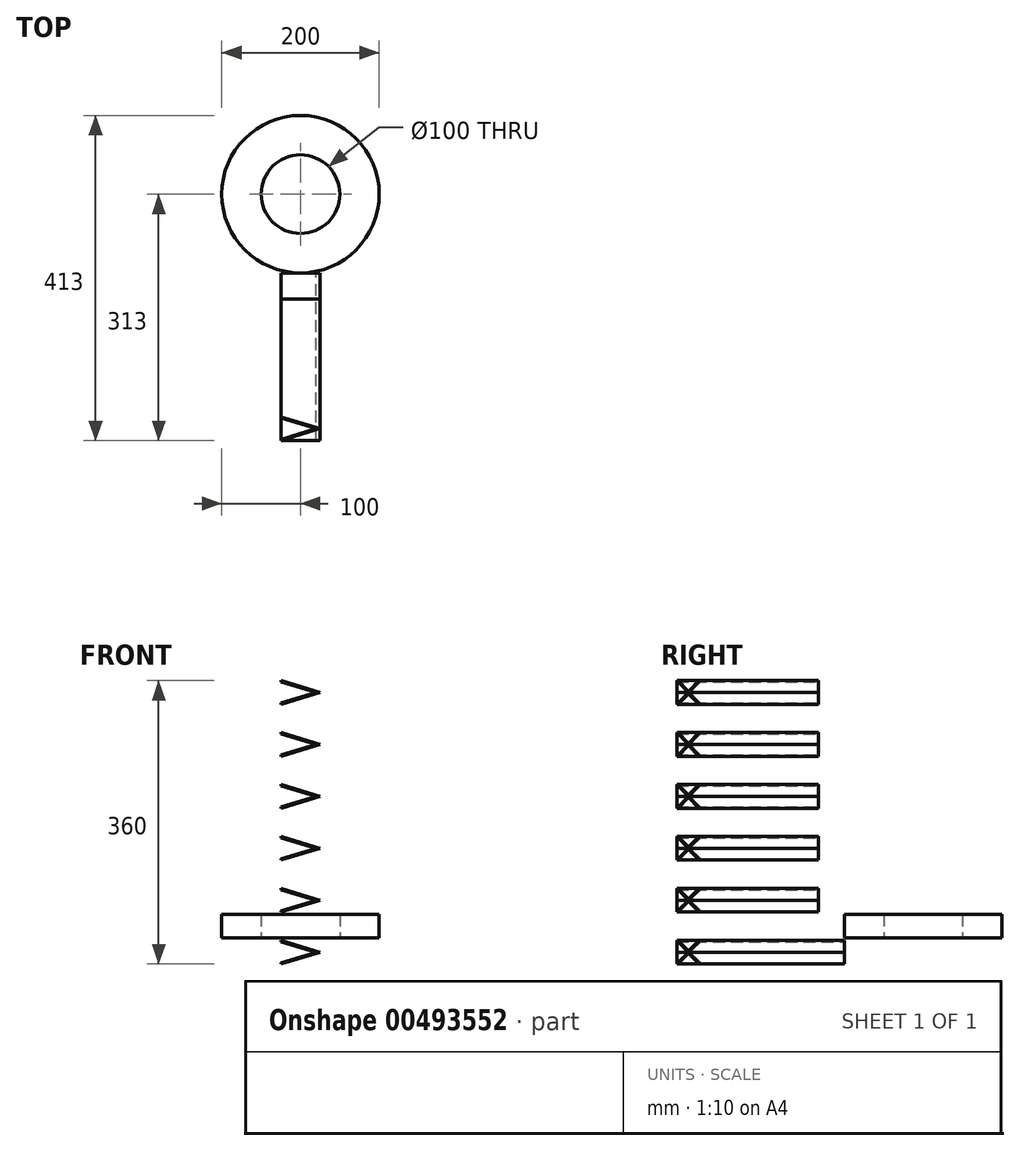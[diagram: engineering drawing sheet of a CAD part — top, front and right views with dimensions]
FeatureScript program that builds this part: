
annotation { "Feature Type Name" : "Feature", "Feature Type Description" : "" }
export const myFeature = defineFeature(function(context is Context, id is Id, definition is map)
    precondition{}
    {
        {
            var Q0;
            Q0=qCreatedBy(makeId("Right.planeOp"),FACE);
            var sketch = newSketch(context, id + "F0", { "sketchPlane" : qUnion([Q0])});
            skLineSegment(sketch, "E0", {"start": v(0, 0) * mm, "end": v(0, 400) * mm});
            skLineSegment(sketch, "E1", {"start": v(0, 0) * mm, "end": v(100, 0) * mm});
            skLineSegment(sketch, "E2", {"start": v(100, 0) * mm, "end": v(100, 360) * mm});
            skLineSegment(sketch, "E3.bottom", {"start": v(100, 360) * mm, "end": v(130, 360) * mm});
            skLineSegment(sketch, "E3.top", {"start": v(100, 0) * mm, "end": v(130, 0) * mm});
            skLineSegment(sketch, "E3.left", {"start": v(100, 360) * mm, "end": v(100, 0) * mm});
            skLineSegment(sketch, "E3.right", {"start": v(130, 360) * mm, "end": v(130, 0) * mm});
            skLineSegment(sketch, "E4.bottom", {"start": v(130, 0) * mm, "end": v(280, 0) * mm});
            skLineSegment(sketch, "E4.top", {"start": v(100, 30) * mm, "end": v(280, 30) * mm});
            skLineSegment(sketch, "E4.left", {"start": v(130, 0) * mm, "end": v(130, 30) * mm});
            skLineSegment(sketch, "E4.right", {"start": v(280, 0) * mm, "end": v(280, 30) * mm});
            skLineSegment(sketch, "E5", {"start": v(280, 66) * mm, "end": v(130, 66) * mm});
            skLineSegment(sketch, "E6", {"start": v(280, 66) * mm, "end": v(280, 96) * mm});
            skLineSegment(sketch, "E7.bottom", {"start": v(280, 96) * mm, "end": v(130, 96) * mm});
            skLineSegment(sketch, "E7.left", {"start": v(280, 96) * mm, "end": v(280, 66) * mm});
            skLineSegment(sketch, "E7.right", {"start": v(130, 96) * mm, "end": v(130, 66) * mm});
            skLineSegment(sketch, "E8.0.1.0", {"start": v(280, 132) * mm, "end": v(130, 132) * mm});
            skLineSegment(sketch, "E8.0.1.1", {"start": v(280, 132) * mm, "end": v(280, 162) * mm});
            skLineSegment(sketch, "E8.0.1.2", {"start": v(130, 162) * mm, "end": v(130, 132) * mm});
            skLineSegment(sketch, "E8.0.1.3", {"start": v(280, 162) * mm, "end": v(130, 162) * mm});
            skLineSegment(sketch, "E8.0.1.4", {"start": v(280, 162) * mm, "end": v(280, 132) * mm});
            skLineSegment(sketch, "E8.0.1.5", {"start": v(280, 132) * mm, "end": v(130, 132) * mm});
            skLineSegment(sketch, "E8.0.2.0", {"start": v(280, 198) * mm, "end": v(130, 198) * mm});
            skLineSegment(sketch, "E8.0.2.1", {"start": v(280, 198) * mm, "end": v(280, 228) * mm});
            skLineSegment(sketch, "E8.0.2.2", {"start": v(130, 228) * mm, "end": v(130, 198) * mm});
            skLineSegment(sketch, "E8.0.2.3", {"start": v(280, 228) * mm, "end": v(130, 228) * mm});
            skLineSegment(sketch, "E8.0.2.4", {"start": v(280, 228) * mm, "end": v(280, 198) * mm});
            skLineSegment(sketch, "E8.0.2.5", {"start": v(280, 198) * mm, "end": v(130, 198) * mm});
            skLineSegment(sketch, "E8.0.3.0", {"start": v(280, 264) * mm, "end": v(130, 264) * mm});
            skLineSegment(sketch, "E8.0.3.1", {"start": v(280, 264) * mm, "end": v(280, 294) * mm});
            skLineSegment(sketch, "E8.0.3.2", {"start": v(130, 294) * mm, "end": v(130, 264) * mm});
            skLineSegment(sketch, "E8.0.3.3", {"start": v(280, 294) * mm, "end": v(130, 294) * mm});
            skLineSegment(sketch, "E8.0.3.4", {"start": v(280, 294) * mm, "end": v(280, 264) * mm});
            skLineSegment(sketch, "E8.0.3.5", {"start": v(280, 264) * mm, "end": v(130, 264) * mm});
            skLineSegment(sketch, "E8.0.4.0", {"start": v(280, 330) * mm, "end": v(100, 330) * mm});
            skLineSegment(sketch, "E8.0.4.1", {"start": v(280, 330) * mm, "end": v(280, 360) * mm});
            skLineSegment(sketch, "E8.0.4.2", {"start": v(130, 360) * mm, "end": v(130, 330) * mm});
            skLineSegment(sketch, "E8.0.4.3", {"start": v(280, 360) * mm, "end": v(130, 360) * mm});
            skLineSegment(sketch, "E8.0.4.4", {"start": v(280, 360) * mm, "end": v(280, 330) * mm});
            skLineSegment(sketch, "E8.0.4.5", {"start": v(280, 330) * mm, "end": v(130, 330) * mm});
            skLineSegment(sketch, "E8.direction1", {"start": v(130, 66) * mm, "end": v(205, 66) * mm, "construction": true});
            skLineSegment(sketch, "E8.direction2", {"start": v(130, 66) * mm, "end": v(130, 132) * mm, "construction": true});
            skLineSegment(sketch, "E9", {"start": v(-100, 363) * mm, "end": v(-283, 363) * mm});
            skLineSegment(sketch, "E10", {"start": v(-100, 363) * mm, "end": v(-100, 393) * mm});
            skLineSegment(sketch, "E11.bottom", {"start": v(-283, 363) * mm, "end": v(-100, 363) * mm});
            skLineSegment(sketch, "E11.top", {"start": v(-313, 393) * mm, "end": v(-100, 393) * mm});
            skLineSegment(sketch, "E12.MirrorCS", {"start": v(-100, -3) * mm, "end": v(-100, -33) * mm});
            skLineSegment(sketch, "E13.MirrorCS", {"start": v(-283, -3) * mm, "end": v(-100, -3) * mm});
            skLineSegment(sketch, "E14.MirrorCS", {"start": v(-100, -3) * mm, "end": v(-283, -3) * mm});
            skLineSegment(sketch, "E15.MirrorCS", {"start": v(-313, -33) * mm, "end": v(-100, -33) * mm});
            skLineSegment(sketch, "E16", {"start": v(-283, 363) * mm, "end": v(-283, 327) * mm});
            skLineSegment(sketch, "E17.0", {"start": v(-133, 297) * mm, "end": v(-283, 297) * mm});
            skLineSegment(sketch, "E18.0", {"start": v(-133, 327) * mm, "end": v(-283, 327) * mm});
            skLineSegment(sketch, "E19.0", {"start": v(-313, 393) * mm, "end": v(-313, -33) * mm});
            skLineSegment(sketch, "E20.0", {"start": v(-133, 327) * mm, "end": v(-133, 297) * mm});
            skLineSegment(sketch, "E21.0.1.1", {"start": v(-133, 261) * mm, "end": v(-283, 261) * mm});
            skLineSegment(sketch, "E21.0.1.2", {"start": v(-133, 231) * mm, "end": v(-283, 231) * mm});
            skLineSegment(sketch, "E21.0.1.3", {"start": v(-133, 261) * mm, "end": v(-133, 231) * mm});
            skLineSegment(sketch, "E21.0.2.1", {"start": v(-133, 195) * mm, "end": v(-283, 195) * mm});
            skLineSegment(sketch, "E21.0.2.2", {"start": v(-133, 165) * mm, "end": v(-283, 165) * mm});
            skLineSegment(sketch, "E21.0.2.3", {"start": v(-133, 195) * mm, "end": v(-133, 165) * mm});
            skLineSegment(sketch, "E21.0.3.1", {"start": v(-133, 129) * mm, "end": v(-283, 129) * mm});
            skLineSegment(sketch, "E21.0.3.2", {"start": v(-133, 99) * mm, "end": v(-283, 99) * mm});
            skLineSegment(sketch, "E21.0.3.3", {"start": v(-133, 129) * mm, "end": v(-133, 99) * mm});
            skLineSegment(sketch, "E21.0.4.1", {"start": v(-133, 63) * mm, "end": v(-283, 63) * mm});
            skLineSegment(sketch, "E21.0.4.2", {"start": v(-133, 33) * mm, "end": v(-283, 33) * mm});
            skLineSegment(sketch, "E21.0.4.3", {"start": v(-133, 63) * mm, "end": v(-133, 33) * mm});
            skLineSegment(sketch, "E21.direction1", {"start": v(-283, 297) * mm, "end": v(-258, 297) * mm, "construction": true});
            skLineSegment(sketch, "E21.direction2", {"start": v(-283, 297) * mm, "end": v(-283, 261) * mm, "construction": true});
            skLineSegment(sketch, "E22.trimOffspring", {"start": v(-283, 297) * mm, "end": v(-283, 261) * mm});
            skLineSegment(sketch, "E23.trimOffspring", {"start": v(-283, 231) * mm, "end": v(-283, 195) * mm});
            skLineSegment(sketch, "E24.trimOffspring", {"start": v(-283, 165) * mm, "end": v(-283, 129) * mm});
            skLineSegment(sketch, "E25.trimOffspring", {"start": v(-283, 99) * mm, "end": v(-283, 63) * mm});
            skLineSegment(sketch, "E26.trimOffspring", {"start": v(-283, 33) * mm, "end": v(-283, -3) * mm});
            skSolve(sketch);
        }
        {
            var Q0;
            Q0=qSketchRegion(id+"F0",true);
            extrude(context, id + "F1", {"entities" : qUnion([Q0]), "endBound" : BoundingType.SYMMETRIC, "depth" : 50 * mm, "offsetDistance" : 25 * mm});
        }
        {
            var Q0;
            Q0=makeQuery(id+"F1.opExtrude","SWEPT_FACE",FACE,{"disambiguationData":[OSD([sQuery(id+"F0.wireOp",EDGE,"E10")])]});
            var sketch = newSketch(context, id + "F2", { "sketchPlane" : qUnion([Q0])});
            skLineSegment(sketch, "E27", {"start": v(-25, 378) * mm, "end": v(25, 393) * mm});
            skLineSegment(sketch, "E28", {"start": v(25, 393) * mm, "end": v(-25, 378) * mm});
            skLineSegment(sketch, "E29", {"start": v(25, 363) * mm, "end": v(-25, 378) * mm});
            skLineSegment(sketch, "E30.0", {"start": v(25.43, 364.44) * mm, "end": v(-19.78, 378) * mm});
            skLineSegment(sketch, "E31.trimOffspring", {"start": v(-19.78, 378) * mm, "end": v(25.43, 391.56) * mm});
            skSolve(sketch);
        }
        {
            var Q0;
            Q0=makeQuery(id+"F1.opExtrude","SWEPT_FACE",FACE,{"disambiguationData":[OSD([sQuery(id+"F0.wireOp",EDGE,"E11.top")])]});
            var sketch = newSketch(context, id + "F3", { "sketchPlane" : qUnion([Q0])});
            skLineSegment(sketch, "E32", {"start": v(25, -298) * mm, "end": v(-25, -313) * mm});
            skLineSegment(sketch, "E33", {"start": v(25, -298) * mm, "end": v(-25, -283) * mm});
            skLineSegment(sketch, "E34.trimOffspring", {"start": v(19.78, -298) * mm, "end": v(-25.43, -284.44) * mm});
            skLineSegment(sketch, "E35.trimOffspring", {"start": v(19.78, -298) * mm, "end": v(-25.43, -311.56) * mm});
            skSolve(sketch);
        }
        {
            var Q0;
            Q0=makeQuery(id+"F1.opExtrude","SWEPT_FACE",FACE,{"disambiguationData":[OSD([sQuery(id+"F0.wireOp",EDGE,"E20.0")])]});
            var sketch = newSketch(context, id + "F4", { "sketchPlane" : qUnion([Q0])});
            skLineSegment(sketch, "E36", {"start": v(-25, 312) * mm, "end": v(25, 327) * mm});
            skLineSegment(sketch, "E37", {"start": v(-25, 312) * mm, "end": v(25, 297) * mm});
            skLineSegment(sketch, "E38.trimOffspring", {"start": v(-19.78, 312) * mm, "end": v(25.43, 298.44) * mm});
            skLineSegment(sketch, "E39.trimOffspring", {"start": v(-19.78, 312) * mm, "end": v(25.43, 325.56) * mm});
            skSolve(sketch);
        }
        {
            var Q0;
            {var subQ8=sQuery(id+"F3.wireOp",EDGE,"E32");Q0=makeQuery(id+"F3.imprint","IMPRINT",FACE,{"disambiguationData":[TD([[makeQuery(id+"F3.imprint","IMPRINT",EDGE,{"derivedFrom":subQ8}),-1.0]])]});}
            var Q1;
            Q1=makeQuery(id+"F1.opExtrude","SWEPT_FACE",FACE,{"disambiguationData":[OSD([sQuery(id+"F0.wireOp",EDGE,"E15.MirrorCS")])]});
            extrude(context, id + "F5", {"entities" : qUnion([Q0]), "endBound" : BoundingType.UP_TO_SURFACE, "oppositeDirection" : true, "depth" : 25 * mm, "endBoundEntityFace" : qUnion([Q1]), "offsetDistance" : 25 * mm});
        }
        {
            var Q0;
            Q0=makeQuery(id+"F1.opExtrude","SWEPT_FACE",FACE,{"disambiguationData":[OSD([sQuery(id+"F0.wireOp",EDGE,"E21.0.1.3")])]});
            var sketch = newSketch(context, id + "F6", { "sketchPlane" : qUnion([Q0])});
            skLineSegment(sketch, "E40", {"start": v(-25, 246) * mm, "end": v(25, 261) * mm});
            skLineSegment(sketch, "E41", {"start": v(-25, 246) * mm, "end": v(25, 231) * mm});
            skLineSegment(sketch, "E42.0", {"start": v(-19.78, 246) * mm, "end": v(25.43, 259.56) * mm});
            skLineSegment(sketch, "E43.0", {"start": v(-19.78, 246) * mm, "end": v(25.43, 232.44) * mm});
            skSolve(sketch);
        }
        {
            var Q0;
            Q0=makeQuery(id+"F1.opExtrude","SWEPT_FACE",FACE,{"disambiguationData":[OSD([sQuery(id+"F0.wireOp",EDGE,"E21.0.2.3")])]});
            var sketch = newSketch(context, id + "F7", { "sketchPlane" : qUnion([Q0])});
            skLineSegment(sketch, "E44", {"start": v(-25, 180) * mm, "end": v(25, 195) * mm});
            skLineSegment(sketch, "E45", {"start": v(-25, 180) * mm, "end": v(25, 165) * mm});
            skLineSegment(sketch, "E46.0", {"start": v(-19.78, 180) * mm, "end": v(25.43, 193.56) * mm});
            skLineSegment(sketch, "E47.0", {"start": v(-19.78, 180) * mm, "end": v(25.43, 166.44) * mm});
            skSolve(sketch);
        }
        {
            var Q0;
            Q0=makeQuery(id+"F1.opExtrude","SWEPT_FACE",FACE,{"disambiguationData":[OSD([sQuery(id+"F0.wireOp",EDGE,"E21.0.3.3")])]});
            var sketch = newSketch(context, id + "F8", { "sketchPlane" : qUnion([Q0])});
            skLineSegment(sketch, "E48", {"start": v(25, 129) * mm, "end": v(-25, 114) * mm});
            skLineSegment(sketch, "E49", {"start": v(-25, 114) * mm, "end": v(25, 99) * mm});
            skLineSegment(sketch, "E50.0", {"start": v(25.43, 127.56) * mm, "end": v(-19.78, 114) * mm});
            skLineSegment(sketch, "E51.0", {"start": v(-19.78, 114) * mm, "end": v(25.43, 100.44) * mm});
            skSolve(sketch);
        }
        {
            var Q0;
            Q0=makeQuery(id+"F1.opExtrude","SWEPT_FACE",FACE,{"disambiguationData":[OSD([sQuery(id+"F0.wireOp",EDGE,"E21.0.4.3")])]});
            var sketch = newSketch(context, id + "F9", { "sketchPlane" : qUnion([Q0])});
            skLineSegment(sketch, "E52", {"start": v(25, 63) * mm, "end": v(-25, 48) * mm});
            skLineSegment(sketch, "E53", {"start": v(-25, 48) * mm, "end": v(25, 33) * mm});
            skLineSegment(sketch, "E54.0", {"start": v(25.43, 61.56) * mm, "end": v(-19.78, 48) * mm});
            skLineSegment(sketch, "E55.0", {"start": v(-19.78, 48) * mm, "end": v(25.43, 34.44) * mm});
            skSolve(sketch);
        }
        {
            var Q0;
            Q0=makeQuery(id+"F1.opExtrude","SWEPT_FACE",FACE,{"disambiguationData":[OSD([sQuery(id+"F0.wireOp",EDGE,"E12.MirrorCS")])]});
            var sketch = newSketch(context, id + "F10", { "sketchPlane" : qUnion([Q0])});
            skLineSegment(sketch, "E56", {"start": v(25, -3) * mm, "end": v(-25, -18) * mm});
            skLineSegment(sketch, "E57", {"start": v(-25, -18) * mm, "end": v(25, -33) * mm});
            skLineSegment(sketch, "E58.0", {"start": v(25.43, -4.44) * mm, "end": v(-19.78, -18) * mm});
            skLineSegment(sketch, "E59.0", {"start": v(-19.78, -18) * mm, "end": v(25.43, -31.56) * mm});
            skSolve(sketch);
        }
        {
            var Q0;
            {var subQ8=sQuery(id+"F2.wireOp",EDGE,"E28");Q0=makeQuery(id+"F2.imprint","IMPRINT",FACE,{"disambiguationData":[TD([[makeQuery(id+"F2.imprint","IMPRINT",EDGE,{"derivedFrom":subQ8}),1.0]])]});}
            var Q1;
            {var subQ8=sQuery(id+"F4.wireOp",EDGE,"E36");Q1=makeQuery(id+"F4.imprint","IMPRINT",FACE,{"disambiguationData":[TD([[makeQuery(id+"F4.imprint","IMPRINT",EDGE,{"derivedFrom":subQ8}),-1.0]])]});}
            var Q2;
            {var subQ8=sQuery(id+"F6.wireOp",EDGE,"E40");Q2=makeQuery(id+"F6.imprint","IMPRINT",FACE,{"disambiguationData":[TD([[makeQuery(id+"F6.imprint","IMPRINT",EDGE,{"derivedFrom":subQ8}),-1.0]])]});}
            var Q3;
            {var subQ8=sQuery(id+"F7.wireOp",EDGE,"E44");Q3=makeQuery(id+"F7.imprint","IMPRINT",FACE,{"disambiguationData":[TD([[makeQuery(id+"F7.imprint","IMPRINT",EDGE,{"derivedFrom":subQ8}),-1.0]])]});}
            var Q4;
            {var subQ8=sQuery(id+"F8.wireOp",EDGE,"E48");Q4=makeQuery(id+"F8.imprint","IMPRINT",FACE,{"disambiguationData":[TD([[makeQuery(id+"F8.imprint","IMPRINT",EDGE,{"derivedFrom":subQ8}),1.0]])]});}
            var Q5;
            {var subQ8=sQuery(id+"F9.wireOp",EDGE,"E52");Q5=makeQuery(id+"F9.imprint","IMPRINT",FACE,{"disambiguationData":[TD([[makeQuery(id+"F9.imprint","IMPRINT",EDGE,{"derivedFrom":subQ8}),1.0]])]});}
            var Q6;
            {var subQ8=sQuery(id+"F10.wireOp",EDGE,"E56");Q6=makeQuery(id+"F10.imprint","IMPRINT",FACE,{"disambiguationData":[TD([[makeQuery(id+"F10.imprint","IMPRINT",EDGE,{"derivedFrom":subQ8}),1.0]])]});}
            var Q7;
            Q7=makeQuery(id+"F1.opExtrude","SWEPT_FACE",FACE,{"disambiguationData":[OSD([sQuery(id+"F0.wireOp",EDGE,"E19.0")])]});
            var Q8;
            Q8=makeQuery(id+"F5.opExtrude","CAP_VERTEX",VERTEX,{"disambiguationData":[OSD([sQuery(id+"F0.wireOp",EDGE,"E11.top"),sQuery(id+"F3.wireOp",EDGE,"E32"),sQuery(id+"F3.wireOp",EDGE,"E33")])],"isStart":true});
            extrude(context, id + "F11", {"entities" : qUnion([Q0, Q1, Q2, Q3, Q4, Q5, Q6]), "operationType" : NewBodyOperationType.INTERSECT, "endBound" : BoundingType.UP_TO_SURFACE, "oppositeDirection" : true, "depth" : 25 * mm, "endBoundEntityFace" : qUnion([Q7]), "endBoundEntityVertex" : qUnion([Q8]), "offsetDistance" : 25 * mm});
        }
        {
            var Q0;
            Q0=qCreatedBy(makeId("Top.planeOp"),FACE);
            var sketch = newSketch(context, id + "F12", { "sketchPlane" : qUnion([Q0])});
            skCircle(sketch, "E60", {"center": v(0, 0) * mm, "radius": 100 * mm});
            skCircle(sketch, "E61", {"center": v(0, 0) * mm, "radius": 50 * mm});
            skSolve(sketch);
        }
        {
            var Q0;
            Q0=makeQuery(id+"F12.imprint","IMPRINT",FACE,{"disambiguationData":[TD([[makeQuery(id+"F12.imprint","IMPRINT",EDGE,{"derivedFrom":sQuery(id+"F12.wireOp",EDGE,"E60")}),1.0]])]});
            extrude(context, id + "F13", {"entities" : qUnion([Q0]), "operationType" : NewBodyOperationType.ADD, "depth" : 30 * mm, "offsetDistance" : 25 * mm});
        }
    });
